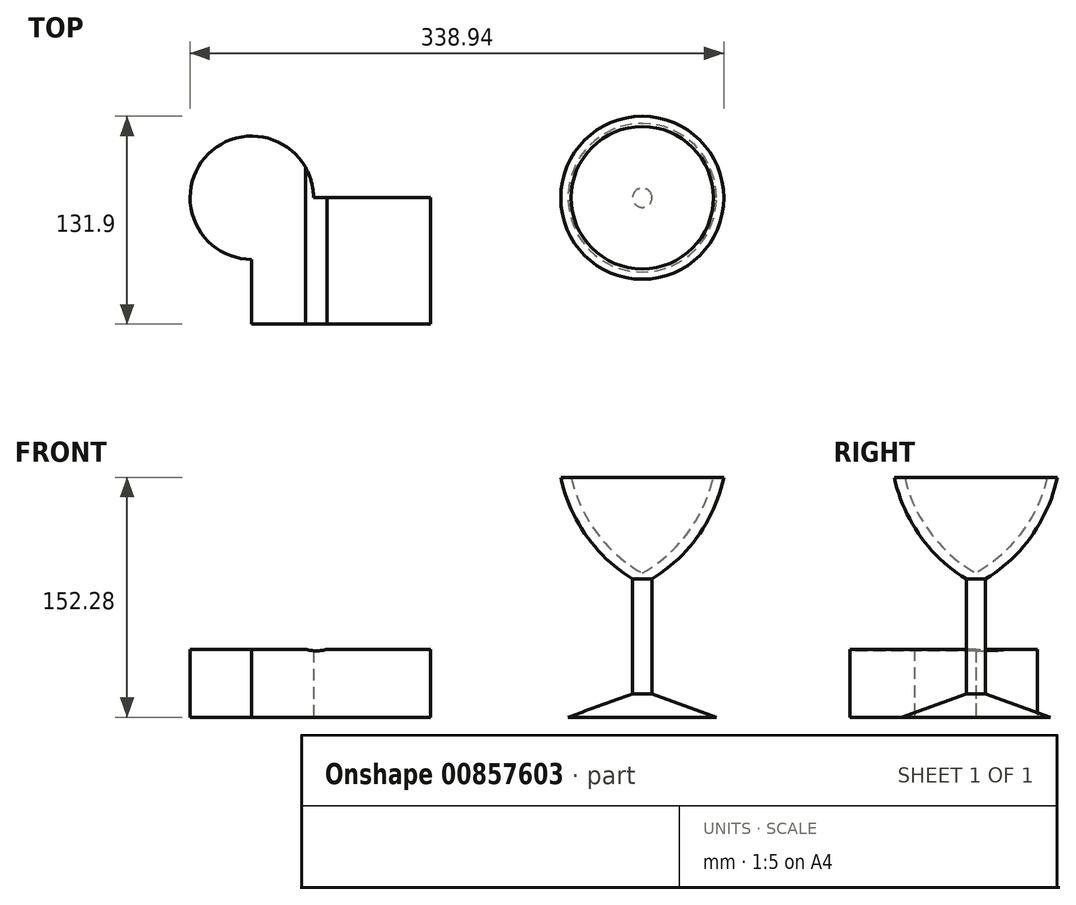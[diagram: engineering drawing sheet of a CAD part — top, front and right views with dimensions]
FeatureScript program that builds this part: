
annotation { "Feature Type Name" : "Feature", "Feature Type Description" : "" }
export const myFeature = defineFeature(function(context is Context, id is Id, definition is map)
    precondition{}
    {
        {
            var Q0;
            Q0=qCreatedBy(makeId("Front.planeOp"),FACE);
            var sketch = newSketch(context, id + "F0", { "sketchPlane" : qUnion([Q0])});
            skLineSegment(sketch, "E0", {"start": v(-124.19, -75.5) * mm, "end": v(-124.19, 16.03) * mm});
            skArc(sketch, "E1", {"start": v(-169.37, 76.78) * mm, "mid": v(-153.15, 41.67) * mm, "end": v(-124.19, 16.03) * mm});
            skArc(sketch, "E2", {"start": v(-175.93, 76.78) * mm, "mid": v(-159.73, 39.85) * mm, "end": v(-130.34, 12.25) * mm});
            skLineSegment(sketch, "E3", {"start": v(-130.34, 12.25) * mm, "end": v(-130.34, -60.74) * mm});
            skLineSegment(sketch, "E4", {"start": v(-130.34, -60.74) * mm, "end": v(-171.37, -75.5) * mm});
            skLineSegment(sketch, "E5", {"start": v(-171.37, -75.5) * mm, "end": v(-124.19, -75.5) * mm});
            skLineSegment(sketch, "E6", {"start": v(-175.93, 76.78) * mm, "end": v(-169.37, 76.78) * mm});
            skSolve(sketch);
        }
        {
            var Q0;
            Q0 = qSketchRegion(id + "F0", true);
            var Q1;
            Q1=sQuery(id+"F0.wireOp",EDGE,"E0");
            revolve(context, id + "F1", {"surfaceOperationType" : NewSurfaceOperationType.NEW, "entities" : qUnion([Q0]), "axis" : qUnion([Q1]), "revolveType" : RevolveType.FULL});
        }
        {
            var Q0;
            Q0=makeQuery(id+"F1.opRevolve","SWEPT_FACE",FACE,{"disambiguationData":[OSD([sQuery(id+"F0.wireOp",EDGE,"E5")])]});
            var sketch = newSketch(context, id + "F2", { "sketchPlane" : qUnion([Q0])});
            skLineSegment(sketch, "E7.bottom", {"start": v(-372.2, 0) * mm, "end": v(-258.8, 0) * mm});
            skLineSegment(sketch, "E7.top", {"start": v(-372.2, 80.16) * mm, "end": v(-258.8, 80.16) * mm});
            skLineSegment(sketch, "E7.left", {"start": v(-372.2, 0) * mm, "end": v(-372.2, 80.16) * mm});
            skLineSegment(sketch, "E7.right", {"start": v(-258.8, 0) * mm, "end": v(-258.8, 80.16) * mm});
            skCircle(sketch, "E8", {"center": v(-372.2, 0) * mm, "radius": 39.19 * mm});
            skSolve(sketch);
        }
        {
            var Q0;
            Q0 = qSketchRegion(id + "F2", true);
            extrude(context, id + "F3", {"entities" : qUnion([Q0]), "oppositeDirection" : true, "depth" : 43.18 * mm, "offsetDistance" : 25.4 * mm});
        }
        {
            var Q0;
            Q0=makeQuery(id+"F3.opExtrude","SWEPT_FACE",FACE,{"disambiguationData":[OSD([sQuery(id+"F2.wireOp",EDGE,"E7.top")])]});
            var sketch = newSketch(context, id + "F4", { "sketchPlane" : qUnion([Q0])});
            skCircle(sketch, "E9", {"center": v(-331.2, -9.7) * mm, "radius": 23.66 * mm});
            skSolve(sketch);
        }
        {
            var Q0;
            Q0 = qSketchRegion(id + "F4", true);
            extrude(context, id + "F5", {"entities" : qUnion([Q0]), "operationType" : NewBodyOperationType.REMOVE, "oppositeDirection" : true, "depth" : 198.12 * mm, "offsetDistance" : 25.4 * mm});
        }
    });
